# Revit family: QF-Repressurization_Pump-OptiPure-HF+-1HP
name_source: partatom
category: Specialty Equipment
revit_build: Autodesk Revit 2017 (Build: 20160225_1515(x64)
units: mm (PartAtom-declared; Revit-internal decimal feet)

## family parameters
Always vertical = Yes
Cut with Voids When Loaded = No
OmniClass Number = 23.40.40.14
OmniClass Title = Food Service Equipment
Part Type = Normal
Room Calculation Point = No
Round Connector Dimension = Use Diameter
Shared = No
Work Plane-Based = No

## types (1)
- HF PLUS - 1 HP
    Assembly Code = E1090300
    Body Material = Black Plastic
    Current = 8 A
    Cycle = 60 Hz
    Description = REPRESSURIZATION PUMP
    Filtered Water In A = 0.5 "
    Filtered Water Out A = 0.5 "
    Height = 16.34 "
    Keynote = 11400
    Length = 24.47 "
    Manufacturer = OPTIPURE
    Material = Stainless Steel
    Model = 164-85100 - SMART PUMP ASSY HF PLUS - 1 HP
    URL = WWW.OPTIPUREWATER.COM
    Volts = 120 V
    Watts = 2 W
    Width = 8.5 "

## geometry (parser evidence)
native form markers: Sweep x4
no freeform markers — native parametric forms only
